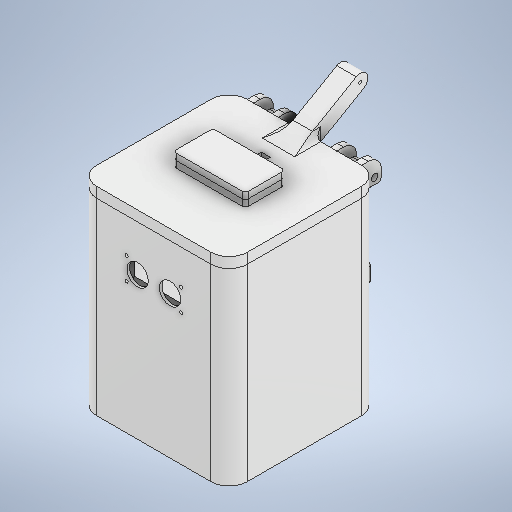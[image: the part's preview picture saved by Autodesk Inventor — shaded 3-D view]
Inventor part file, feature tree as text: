
AUTODESK INVENTOR PART (.ipt)
format: ipt  version: 2025.2 (Build 292293000, 293)  size: 1,300,992 bytes
history: native  units: mm
features: sketch x58, extrude x52, fillet x17, other x6
ambient origin geometry x8: Origin, YZ Plane, XZ Plane, XY Plane, X Axis, Y Axis, Z Axis, Center Point
bodies: Body1 (feature_tree), Body2 (feature_tree), Body3 (feature_tree), Body4 (feature_tree), Body5 (feature_tree), Body6 (feature_tree)
feature tree (133):
  other  "Main_Body"
  extrude  "Extrusão1"  Depth=116.0mm
  extrude  "Extrusão2"  Depth=145.0mm
  extrude  "Extrusão3"  Depth=140.0mm TaperAngle=0.0deg
  sketch  "Esboço4"  dims[d10=22.75mm d11=20.5mm]
  extrude  "Extrusão4"  Depth=22.75mm
  extrude  "Extrusão5"  Depth=22.75mm
  extrude  "Extrusão6"  Depth=8.0mm
  extrude  "Extrusão7"  Depth=2.0mm TaperAngle=0.0deg
  extrude  "Extrusão8"  Depth=25.0mm
  extrude  "Extrusão9"  Depth=16.5mm
  extrude  "Extrusão10"  Depth=1.75mm
  extrude  "Extrusão11"  Depth=1.75mm
  sketch  "Esboço13"  dims[d30=2.5mm d31=2.0mm d32=0.0mm]
  extrude  "Extrusão12"  Depth=2.5mm
  extrude  "Extrusão13"  Depth=2.5mm
  extrude  "Extrusão14"  Depth=2.0mm TaperAngle=0.0deg
  extrude  "Extrusão15"  Depth=7.0mm
  sketch  "Esboço18"  dims[d42=50.0mm d43=0.0mm d44=50.0mm d45=0.0mm]
  extrude  "Extrusão16"  Depth=14.0mm
  sketch  "Esboço20"  dims[d49=14.0mm d50=7.0mm d51=0.0mm]
  sketch  "Esboço21"  dims[d52=10.0mm d53=3.0mm]
  extrude  "Extrusão17"  Depth=14.0mm
  extrude  "Extrusão18"  Depth=10.0mm TaperAngle=0.0deg
  extrude  "Extrusão19"  Depth=50.0mm TaperAngle=0.0deg
  extrude  "Extrusão21"  Depth=7.0mm
  sketch  "Esboço25"  dims[d61=15.0mm d62=14.0mm d63=14.0mm]
  sketch  "Esboço 3D1"  dims[d0=116.0mm d1=116.0mm]
  fillet  "Arredondamento2"  Radius=14.0mm
  extrude  "Extrusão22"  Depth=7.0mm TaperAngle=0.0deg
  extrude  "Extrusão23"  Depth=3.0mm
  extrude  "Extrusão24"  Depth=10.0mm
  fillet  "Arredondamento3"  Radius=12.0mm
  sketch  "Esboço32"  dims[d73=14.0mm d74=14.0mm]
  extrude  "Extrusão27"  Depth=145.0mm
  extrude  "Extrusão28"  Depth=14.0mm
  fillet  "Arredondamento4"  Radius=14.0mm
  extrude  "Extrusão29"  Depth=7.0mm
  extrude  "Extrusão30"  Depth=8.0mm
  fillet  "Arredondamento5"  Radius=145.0mm
  extrude  "Extrusão33"  Depth=7.0mm
  extrude  "Extrusão34"  Depth=14.0mm
  extrude  "Extrusão35"  Depth=7.0mm TaperAngle=0.0deg
  extrude  "Extrusão36"  Depth=7.0mm TaperAngle=0.0deg
  fillet  "Arredondamento7"  Radius=3.0mm
  extrude  "Extrusão37"  Depth=3.0mm
  sketch  "Esboço44"  dims[d108=10.0mm d109=0.0mm d110=45.5mm]
  sketch  "Esboço45"  dims[d111=20.5mm d112=8.0mm d113=0.0mm]
  extrude  "Extrusão38"  Depth=12.0mm TaperAngle=0.0deg
  extrude  "Extrusão39"  Depth=3.0mm
  extrude  "Extrusão40"  Depth=12.0mm TaperAngle=0.0deg
  extrude  "Extrusão42"  Depth=10.0mm
  fillet  "Arredondamento8"  Radius=14.0mm
  fillet  "Arredondamento9"  Radius=2.0mm
  extrude  "Extrusão43"  Depth=3.0mm
  extrude  "Extrusão47"  Depth=10.0mm
  extrude  "Extrusão48"  Depth=10.0mm
  extrude  "Extrusão53"  Depth=8.0mm TaperAngle=0.0deg
  extrude  "Extrusão54"  Depth=25.0mm
  extrude  "Extrusão55"  Depth=16.5mm
  extrude  "Extrusão56"  Depth=1.75mm
  extrude  "Extrusão57"  Depth=1.75mm
  extrude  "Extrusão58"  Depth=2.5mm
  extrude  "Extrusão59"  Depth=2.0mm TaperAngle=0.0deg
  fillet  "Arredondamento11"  Radius=14.0mm
  fillet  "Arredondamento12"  Radius=2.0mm
  fillet  "Arredondamento14"  Radius=14.0mm
  extrude  "Extrusão61"  Depth=7.0mm
  fillet  "Arredondamento15"  Radius=7.0mm
  fillet  "Arredondamento17"  Radius=10.0mm
  fillet  "Arredondamento18"  Radius=10.0mm
  extrude  "Extrusão62"  Depth=10.0mm
  extrude  "Extrusão63"  Depth=5.0mm
  extrude  "Extrusão64"  Depth=5.0mm TaperAngle=0.0deg
  extrude  "Extrusão65"  Depth=5.0mm
  fillet  "Arredondamento19"  Radius=2.0mm
  extrude  "Extrusão66"  Depth=2.0mm
  fillet  "Arredondamento20"  Radius=2.0mm
  fillet  "Arredondamento21"  Radius=10.0mm
  fillet  "Arredondamento22"  Radius=2.0mm
  sketch  "Esboço1"  dims[d2=145.0mm d3=0.0mm d4=100.0mm]
  sketch  "Esboço2"  dims[d5=100.0mm d6=140.0mm d7=0.0mm]
  sketch  "Esboço3"  dims[d8=25.0mm d9=22.75mm]
  sketch  "Esboço5"  dims[d12=8.0mm d13=0.0mm d14=20.5mm]
  sketch  "Esboço6"  dims[d15=2.0mm d16=45.5mm d17=0.0mm]
  sketch  "Esboço7"  dims[d18=12.5mm d19=25.0mm]
  sketch  "Esboço8"  dims[d20=16.5mm d21=16.5mm]
  sketch  "Esboço9"  dims[d22=1.75mm d23=1.75mm]
  sketch  "Esboço10"  dims[d24=1.75mm d25=1.75mm]
  sketch  "Esboço11"  dims[d26=1.75mm d27=2.5mm]
  sketch  "Esboço12"  dims[d28=2.5mm d29=2.5mm]
  sketch  "Esboço14"  dims[d33=15.0mm d34=7.0mm]
  sketch  "Esboço15"  dims[d35=14.0mm d36=20.0mm]
  sketch  "Esboço16"  dims[d37=10.0mm d38=14.0mm]
  sketch  "Esboço17"  dims[d39=10.0mm d40=50.0mm d41=0.0mm]
  sketch  "Esboço19"  dims[d46=15.0mm d47=7.0mm d48=14.0mm]
  sketch  "Esboço23"  dims[d54=12.0mm d55=0.0mm d56=10.0mm d57=12.0mm d58=0.0mm]
  sketch  "Esboço24"  dims[d59=8.0mm d60=145.0mm]
  sketch  "Esboço26"  dims[d64=7.0mm d65=0.0mm d66=7.0mm]
  other  "Main_Lid"
  sketch  "Esboço27"  dims[d67=7.0mm d68=0.0mm d69=8.0mm d70=145.0mm]
  sketch  "Esboço28"  dims[d71=60.5mm d72=7.0mm]
  sketch  "Esboço33"  dims[d75=14.0mm d76=7.0mm d77=0.0mm]
  sketch  "Esboço34"  dims[d78=7.0mm d79=7.0mm d80=0.0mm d81=3.0mm]
  sketch  "Esboço35"  dims[d82=10.0mm d83=3.0mm]
  sketch  "Esboço36"  dims[d84=10.0mm d85=12.0mm d86=0.0mm]
  sketch  "Esboço39"  dims[d87=3.0mm d88=3.0mm]
  sketch  "Esboço40"  dims[d89=12.0mm d90=0.0mm d91=12.0mm d92=0.0mm]
  other  "Sensor_Cover"
  sketch  "Esboço41"  dims[d95=3.0mm d96=10.0mm d97=14.0mm d98=0.0mm d101=2.0mm]
  sketch  "Esboço42"  dims[d102=2.0mm d103=3.0mm]
  sketch  "Esboço43"  dims[d104=10.0mm d105=0.0mm d107=10.0mm]
  other  "Lid_Axis"
  sketch  "Esboço46"  dims[d114=12.5mm d115=25.0mm]
  sketch  "Esboço48"  dims[d116=16.5mm d117=16.5mm]
  sketch  "Esboço49"  dims[d118=1.75mm d119=1.75mm]
  sketch  "Esboço53"  dims[d120=1.75mm d121=1.75mm]
  sketch  "Esboço54"  dims[d122=2.5mm d123=2.5mm]
  sketch  "Esboço59"  dims[d124=2.5mm d125=2.0mm d126=0.0mm d127=14.0mm d158=2.0mm d159=14.0mm]
  sketch  "Esboço60"  dims[d160=2.0mm d161=0.0mm d162=7.0mm d163=7.0mm d164=10.0mm d165=10.0mm]
  sketch  "Esboço61"  dims[d166=10.0mm d167=10.0mm]
  other  "Rear_CableGuide"
  sketch  "Esboço62"  dims[d168=15.0mm d169=0.0mm d170=5.0mm]
  sketch  "Esboço63"  dims[d171=5.0mm d172=115.0mm d173=0.0mm]
  sketch  "Esboço64"  dims[d174=5.0mm d175=5.0mm d176=2.0mm]
  sketch  "Esboço65"  dims[d177=10.0mm d178=2.0mm d179=2.0mm d180=10.0mm d181=2.0mm]
  sketch  "Esboço67"  dims[d182=5.0mm]
  sketch  "Esboço69"  dims[d183=5.0mm]
  sketch  "Esboço70"  dims[d184=15.0mm d185=0.0mm]
  sketch  "Esboço71"  dims[d195=10.0mm]
  other  "Lid_CableGuide"
  sketch  "Esboço72"  dims[d197=55.5mm]
  sketch  "Esboço73"  dims[d198=30.5mm d199=15.0mm d200=3.0mm d201=3.0mm d202=5.0mm d203=0.0mm d204=5.0mm d205=0.0mm d206=45.5mm d207=20.5mm d208=2.5mm d209=2.5mm d210=0.0mm d211=5.0mm d212=0.0mm d213=2.5mm d220=42.5mm d221=3.1mm d222=4.15mm d223=4.3mm d224=2.5mm d225=10.0mm d226=2.5mm d227=10.0mm d228=2.8mm d229=4.0mm d230=2.5mm d231=10.0mm d232=2.8mm d233=4.0mm d234=2.5mm d235=12.5mm d236=0.0mm d237=2.65mm d238=2.7mm d239=2.65mm d240=2.7mm d241=10.0mm d242=5.0mm d243=0.0mm d244=0.0mm d245=10.0mm d246=5.0mm d247=0.0mm d248=0.0mm d249=10.0mm d250=5.0mm d251=14.0mm d252=5.0mm d253=4.0mm d254=4.0mm d255=4.0mm d256=5.0mm d257=14.0mm d258=5.0mm d259=4.0mm d260=4.0mm d261=4.0mm d262=4.0mm d263=5.0mm d264=0.0mm d275=5.0mm d276=10.0mm d277=5.0mm d278=10.0mm d279=5.0mm d280=10.0mm d281=5.0mm d282=10.0mm d283=10.0mm d284=0.0mm d285=2.0mm d286=5.0mm d287=100.0mm d288=0.0mm d318=3.9mm d319=3.9mm d320=3.9mm d321=3.9mm d322=3.9mm d323=4.8mm d324=0.0mm d325=15.0mm d326=10.0mm d327=3.5mm d328=7.0mm d329=3.0mm d330=8.0mm d331=0.0mm d356=23.25mm d357=7.0mm d358=14.0mm d359=14.0mm d360=14.0mm d361=7.0mm d362=0.0mm d363=10.0mm d364=3.0mm d365=46.5mm d366=0.0mm d367=12.8mm d368=12.8mm d369=14.35mm d370=55.0mm d371=41.5mm d372=83.0mm d373=2.0mm d374=7.0mm d375=0.0mm d376=3.0mm d377=10.0mm d378=12.0mm d379=0.0mm d380=10.0mm d381=3.0mm d382=14.0mm d383=0.0mm d384=4.9mm d385=4.9mm d386=4.9mm d387=0.0mm d388=5.0mm d389=5.0mm d390=5.0mm d391=0.0mm d397=3.9mm d398=2.15mm d400=2.0mm d401=10.0mm d402=55.0mm d403=60.0deg d404=11.928mm d405=5.964mm d406=2.5mm d407=15.0mm d408=0.0mm d409=5.0mm d411=5.0mm d412=37.5mm d413=10.0mm d414=10.0mm d415=2.0mm d416=10.0mm d417=0.0mm d418=8.0mm d419=4.0mm d420=14.0mm d421=10.0mm d422=4.0mm d423=4.0mm d424=4.0mm d425=0.0mm d426=14.0mm d427=10.0mm d428=7.0mm d429=0.0mm d430=10.0mm d431=3.0mm d432=15.0mm d433=0.0mm d434=2.15mm d435=3.8mm d436=3.8mm d437=3.8mm d438=0.0mm d439=14.0mm d440=14.0mm d441=14.0mm d106=0.0mm d140=0.5mm d141=0.872665mm d142=0.5mm d143=0.872665mm d196=0.0mm d273=0.5mm d274=0.872665mm d308=0.5mm d309=0.872665mm d310=0.5mm d311=0.872665mm d337=0.5mm d338=0.872665mm d339=0.5mm d340=0.872665mm d341=0.5mm d342=0.872665mm d343=0.5mm d344=0.872665mm d394=0.5mm d395=0.872665mm d396=0.5mm d410=0.872665mm]
